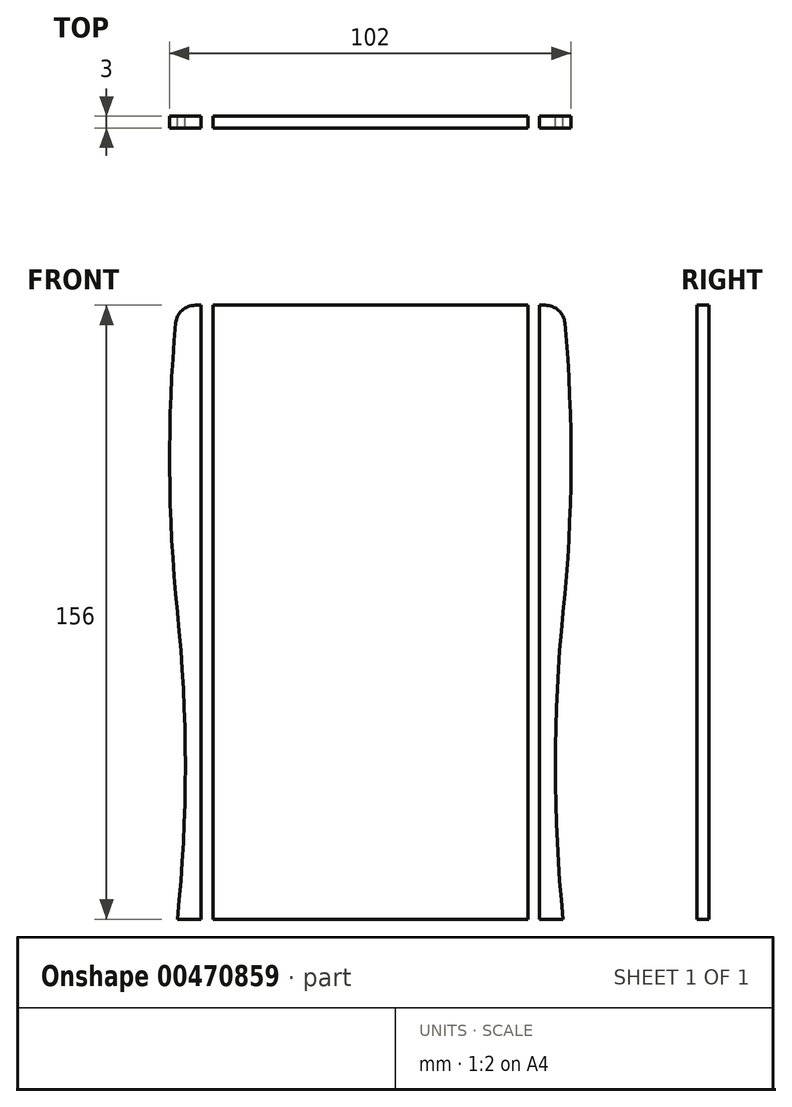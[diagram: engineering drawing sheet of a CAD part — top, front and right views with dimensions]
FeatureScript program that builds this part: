
annotation { "Feature Type Name" : "Feature", "Feature Type Description" : "" }
export const myFeature = defineFeature(function(context is Context, id is Id, definition is map)
    precondition{}
    {
        {
            assignVariable(context, id + "F0", {"name" : "WoodWidth", "anyValue" : 3});
        }
        {
            var Q0;
            Q0=qCreatedBy(makeId("Front.planeOp"),FACE);
            var sketch = newSketch(context, id + "F1", { "sketchPlane" : qUnion([Q0])});
            skLineSegment(sketch, "E0.bottom", {"start": v(49, -78) * mm, "end": v(-49, -78) * mm});
            skLineSegment(sketch, "E0.top", {"start": v(49, 78) * mm, "end": v(-49, 78) * mm});
            skLineSegment(sketch, "E0.left", {"start": v(49, -78) * mm, "end": v(49, 78) * mm});
            skLineSegment(sketch, "E0.right", {"start": v(-49, -78) * mm, "end": v(-49, 78) * mm});
            skPoint(sketch, "E0.middle", {"position": v(0, 0) * mm});
            skLineSegment(sketch, "E1.bottom", {"start": v(-43, -78) * mm, "end": v(-40, -78) * mm});
            skLineSegment(sketch, "E1.top", {"start": v(-43, -3) * mm, "end": v(-40, -3) * mm});
            skLineSegment(sketch, "E1.left", {"start": v(-43, -78) * mm, "end": v(-43, -3) * mm});
            skLineSegment(sketch, "E1.right", {"start": v(-40, -78) * mm, "end": v(-40, -3) * mm});
            skLineSegment(sketch, "E2.bottom", {"start": v(40, -78) * mm, "end": v(43, -78) * mm});
            skLineSegment(sketch, "E2.top", {"start": v(40, -3) * mm, "end": v(43, -3) * mm});
            skLineSegment(sketch, "E2.left", {"start": v(40, -78) * mm, "end": v(40, -3) * mm});
            skLineSegment(sketch, "E2.right", {"start": v(43, -78) * mm, "end": v(43, -3) * mm});
            skLineSegment(sketch, "E3.bottom", {"start": v(-40, -78) * mm, "end": v(-28, -78) * mm});
            skLineSegment(sketch, "E3.top", {"start": v(-40, -81) * mm, "end": v(-28, -81) * mm});
            skLineSegment(sketch, "E3.left", {"start": v(-40, -78) * mm, "end": v(-40, -81) * mm});
            skLineSegment(sketch, "E3.right", {"start": v(-28, -78) * mm, "end": v(-28, -81) * mm});
            skLineSegment(sketch, "E4.bottom", {"start": v(40, -78) * mm, "end": v(28, -78) * mm});
            skLineSegment(sketch, "E4.top", {"start": v(40, -81) * mm, "end": v(28, -81) * mm});
            skLineSegment(sketch, "E4.left", {"start": v(40, -78) * mm, "end": v(40, -81) * mm});
            skLineSegment(sketch, "E4.right", {"start": v(28, -78) * mm, "end": v(28, -81) * mm});
            skLineSegment(sketch, "E5.bottom", {"start": v(-49, -78) * mm, "end": v(-43, -78) * mm});
            skLineSegment(sketch, "E5.top", {"start": v(-49, -81) * mm, "end": v(-43, -81) * mm});
            skLineSegment(sketch, "E5.left", {"start": v(-49, -78) * mm, "end": v(-49, -81) * mm});
            skLineSegment(sketch, "E5.right", {"start": v(-43, -78) * mm, "end": v(-43, -81) * mm});
            skLineSegment(sketch, "E6.bottom", {"start": v(43, -78) * mm, "end": v(49, -78) * mm});
            skLineSegment(sketch, "E6.top", {"start": v(43, -81) * mm, "end": v(49, -81) * mm});
            skLineSegment(sketch, "E6.left", {"start": v(43, -78) * mm, "end": v(43, -81) * mm});
            skLineSegment(sketch, "E6.right", {"start": v(49, -78) * mm, "end": v(49, -81) * mm});
            skLineSegment(sketch, "E7.top", {"start": v(-43, 78) * mm, "end": v(-40, 78) * mm});
            skLineSegment(sketch, "E7.left", {"start": v(-43, -3) * mm, "end": v(-43, 78) * mm});
            skLineSegment(sketch, "E7.right", {"start": v(-40, -3) * mm, "end": v(-40, 78) * mm});
            skLineSegment(sketch, "E8.top", {"start": v(40, 78) * mm, "end": v(43, 78) * mm});
            skLineSegment(sketch, "E8.left", {"start": v(40, -3) * mm, "end": v(40, 78) * mm});
            skLineSegment(sketch, "E8.right", {"start": v(43, -3) * mm, "end": v(43, 78) * mm});
            skLineSegment(sketch, "E9", {"start": v(-43, -81) * mm, "end": v(-40, -81) * mm});
            skLineSegment(sketch, "E10", {"start": v(40, -81) * mm, "end": v(43, -81) * mm});
            skArc(sketch, "E11", {"start": v(-49, 78) * mm, "mid": v(-51, 39) * mm, "end": v(-49, 0) * mm});
            skArc(sketch, "E12", {"start": v(-49, -78) * mm, "mid": v(-47, -39) * mm, "end": v(-49, 0) * mm});
            skArc(sketch, "E13", {"start": v(49, 0) * mm, "mid": v(51, 39) * mm, "end": v(49, 78) * mm});
            skArc(sketch, "E14", {"start": v(49, 0) * mm, "mid": v(47, -39) * mm, "end": v(49, -78) * mm});
            skSolve(sketch);
        }
        {
            var Q0;
            Q0=makeQuery(id+"F1.imprint","IMPRINT",FACE,{"disambiguationData":[TD([[makeQuery(id+"F1.imprint","IMPRINT",EDGE,{"derivedFrom":sQuery(id+"F1.wireOp",EDGE,"E6.bottom")}),-1.0]])]});
            var Q1;
            Q1=makeQuery(id+"F1.imprint","IMPRINT",FACE,{"disambiguationData":[TD([[makeQuery(id+"F1.imprint","IMPRINT",EDGE,{"derivedFrom":sQuery(id+"F1.wireOp",EDGE,"E0.bottom")}),-1.0]])]});
            var Q2;
            Q2=makeQuery(id+"F1.imprint","IMPRINT",FACE,{"disambiguationData":[TD([[makeQuery(id+"F1.imprint","IMPRINT",EDGE,{"derivedFrom":sQuery(id+"F1.wireOp",EDGE,"E5.bottom")}),-1.0]])]});
            var Q3;
            Q3=makeQuery(id+"F1.imprint","IMPRINT",FACE,{"disambiguationData":[TD([[makeQuery(id+"F1.imprint","IMPRINT",EDGE,{"derivedFrom":sQuery(id+"F1.wireOp",EDGE,"E3.bottom")}),-1.0]])]});
            var Q4;
            Q4=makeQuery(id+"F1.imprint","IMPRINT",FACE,{"disambiguationData":[TD([[makeQuery(id+"F1.imprint","IMPRINT",EDGE,{"derivedFrom":sQuery(id+"F1.wireOp",EDGE,"E4.bottom")}),1.0]])]});
            var Q5;
            Q5=makeQuery(id+"F1.imprint","IMPRINT",FACE,{"disambiguationData":[TD([[makeQuery(id+"F1.imprint","IMPRINT",EDGE,{"derivedFrom":sQuery(id+"F1.wireOp",EDGE,"E1.bottom")}),1.0]])]});
            var Q6;
            Q6=makeQuery(id+"F1.imprint","IMPRINT",FACE,{"disambiguationData":[TD([[makeQuery(id+"F1.imprint","IMPRINT",EDGE,{"derivedFrom":sQuery(id+"F1.wireOp",EDGE,"E2.bottom")}),1.0]])]});
            var Q7;
            Q7=makeQuery(id+"F1.imprint","IMPRINT",FACE,{"disambiguationData":[TD([[makeQuery(id+"F1.imprint","IMPRINT",EDGE,{"derivedFrom":sQuery(id+"F1.wireOp",EDGE,"E1.bottom")}),-1.0]])]});
            var Q8;
            Q8=makeQuery(id+"F1.imprint","IMPRINT",FACE,{"disambiguationData":[TD([[makeQuery(id+"F1.imprint","IMPRINT",EDGE,{"derivedFrom":sQuery(id+"F1.wireOp",EDGE,"E2.bottom")}),-1.0]])]});
            var Q9;
            Q9=makeQuery(id+"F1.imprint","IMPRINT",FACE,{"disambiguationData":[TD([[makeQuery(id+"F1.imprint","IMPRINT",EDGE,{"derivedFrom":sQuery(id+"F1.wireOp",EDGE,"E1.left")}),1.0]])]});
            var Q10;
            {var subQ0=sQuery(id+"F1.wireOp",EDGE,"E11");Q10=makeQuery(id+"F1.imprint","IMPRINT",FACE,{"disambiguationData":[TD([[makeQuery(id+"F1.imprint","IMPRINT",EDGE,{"derivedFrom":subQ0}),1.0]])]});}
            var Q11;
            Q11=makeQuery(id+"F1.imprint","IMPRINT",FACE,{"disambiguationData":[TD([[makeQuery(id+"F1.imprint","IMPRINT",EDGE,{"derivedFrom":sQuery(id+"F1.wireOp",EDGE,"E2.right")}),-1.0]])]});
            var Q12;
            {var subQ0=sQuery(id+"F1.wireOp",EDGE,"E13");Q12=makeQuery(id+"F1.imprint","IMPRINT",FACE,{"disambiguationData":[TD([[makeQuery(id+"F1.imprint","IMPRINT",EDGE,{"derivedFrom":subQ0}),1.0]])]});}
            extrude(context, id + "F2", {"entities" : qUnion([Q0, Q1, Q2, Q3, Q4, Q5, Q6, Q7, Q8, Q9, Q10, Q11, Q12]), "depth" : (getVariable(context, 'WoodWidth')) * mm});
        }
        {
            var Q0;
            Q0=makeQuery(id+"F2.opExtrude","SWEPT_EDGE",EDGE,{"disambiguationData":[OSD([sQuery(id+"F1.wireOp",EDGE,"E0.top"),sQuery(id+"F1.wireOp",EDGE,"E0.left")])]});
            var Q1;
            Q1=makeQuery(id+"F2.opExtrude","SWEPT_EDGE",EDGE,{"disambiguationData":[OSD([sQuery(id+"F1.wireOp",EDGE,"E0.top"),sQuery(id+"F1.wireOp",EDGE,"E0.right")])]});
            fillet(context, id + "F3", {"entities" : qUnion([Q0, Q1]), "radius" : 5 * mm, "tangentPropagation" : true, "allowEdgeOverflow" : false});
        }
    });
